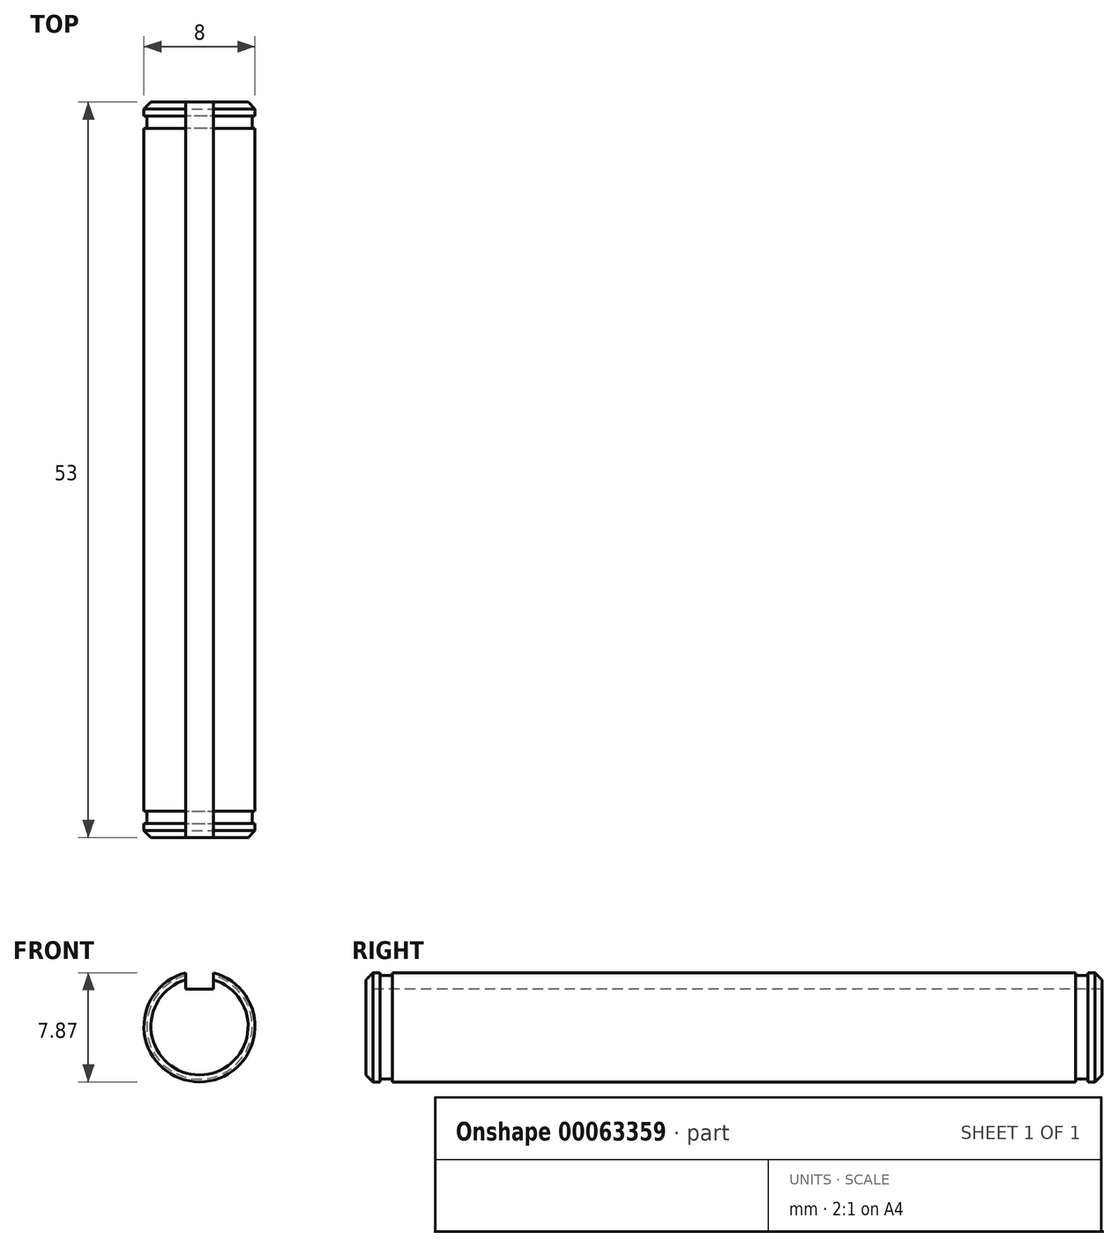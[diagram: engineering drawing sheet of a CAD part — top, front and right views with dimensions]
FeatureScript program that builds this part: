
annotation { "Feature Type Name" : "Feature", "Feature Type Description" : "" }
export const myFeature = defineFeature(function(context is Context, id is Id, definition is map)
    precondition{}
    {
        {
            var Q0;
            Q0=qCreatedBy(makeId("Front.planeOp"),FACE);
            var sketch = newSketch(context, id + "F0", { "sketchPlane" : qUnion([Q0])});
            skCircle(sketch, "E0", {"center": v(0, 0) * mm, "radius": 4 * mm});
            skSolve(sketch);
        }
        {
            var Q0;
            Q0=qSketchRegion(id+"F0",true);
            extrude(context, id + "F1", {"entities" : qUnion([Q0]), "depth" : (48 + 2 * 2.5) * mm});
        }
        {
            var Q0;
            Q0=makeQuery(id+"F1.opExtrude","CAP_FACE",FACE,{"disambiguationData":[OSD([sQuery(id+"F0.wireOp",EDGE,"E0")])],"isStart":false});
            var sketch = newSketch(context, id + "F2", { "sketchPlane" : qUnion([Q0])});
            skLineSegment(sketch, "E1", {"start": v(-1, 5.35) * mm, "end": v(1, 5.35) * mm});
            skLineSegment(sketch, "E2", {"start": v(0, 0) * mm, "end": v(0, 5.35) * mm, "construction": true});
            skLineSegment(sketch, "E3", {"start": v(-1, 2.67) * mm, "end": v(1, 2.67) * mm});
            skPoint(sketch, "E3.startSnap0", {"position": v(0, 2.67) * mm});
            skLineSegment(sketch, "E4", {"start": v(1, 2.67) * mm, "end": v(1, 5.35) * mm});
            skLineSegment(sketch, "E5", {"start": v(-1, 2.67) * mm, "end": v(-1, 5.35) * mm});
            skLineSegment(sketch, "E6", {"start": v(1, 3.87) * mm, "end": v(-1, 3.87) * mm, "construction": true});
            skSolve(sketch);
        }
        {
            var Q0;
            Q0=qSketchRegion(id+"F2",true);
            extrude(context, id + "F3", {"entities" : qUnion([Q0]), "operationType" : NewBodyOperationType.REMOVE, "endBound" : BoundingType.THROUGH_ALL, "oppositeDirection" : true, "depth" : 25 * mm});
        }
        {
            var Q0;
            Q0=makeQuery(id+"F1.opExtrude","CAP_EDGE",EDGE,{"disambiguationData":[OSD([sQuery(id+"F0.wireOp",EDGE,"E0")])],"isStart":false});
            var Q1;
            Q1=makeQuery(id+"F1.opExtrude","CAP_EDGE",EDGE,{"disambiguationData":[OSD([sQuery(id+"F0.wireOp",EDGE,"E0")])],"isStart":true});
            chamfer(context, id + "F4", {"entities" : qUnion([Q0, Q1]), "width" : 0.5 * mm, "tangentPropagation" : true});
        }
        {
            var Q0;
            Q0=makeQuery(id+"F1.opExtrude","CAP_FACE",FACE,{"disambiguationData":[OSD([sQuery(id+"F0.wireOp",EDGE,"E0")])],"isStart":false});
            cPlane(context, id + "F5", {"entities" : qUnion([Q0]), "cplaneType" : CPlaneType.OFFSET, "offset" : 1 * mm, "oppositeDirection" : true, "width" : 150 * mm, "height" : 150 * mm});
        }
        {
            var Q0;
            Q0=qCreatedBy(id+"F5.planeOp",FACE);
            var sketch = newSketch(context, id + "F6", { "sketchPlane" : qUnion([Q0])});
            skCircle(sketch, "E7", {"center": v(0, 0) * mm, "radius": 3.8 * mm});
            skCircle(sketch, "E8", {"center": v(0, 0) * mm, "radius": 5.13 * mm});
            skSolve(sketch);
        }
        {
            var Q0;
            Q0 = qSketchRegion(id + "F6", true);
            extrude(context, id + "F7", {"entities" : qUnion([Q0]), "operationType" : NewBodyOperationType.REMOVE, "oppositeDirection" : true, "depth" : 0.9 * mm});
        }
        {
            var Q0;
            Q0=makeQuery(id+"F1.opExtrude","CAP_FACE",FACE,{"disambiguationData":[OSD([sQuery(id+"F0.wireOp",EDGE,"E0")])],"isStart":true});
            cPlane(context, id + "F8", {"entities" : qUnion([Q0]), "cplaneType" : CPlaneType.OFFSET, "offset" : 1 * mm, "oppositeDirection" : true, "width" : 150 * mm, "height" : 150 * mm});
        }
        {
            var Q0;
            Q0=qCreatedBy(id+"F8.planeOp",FACE);
            var sketch = newSketch(context, id + "F9", { "sketchPlane" : qUnion([Q0])});
            skCircle(sketch, "E9", {"center": v(0, 0) * mm, "radius": 3.8 * mm});
            skCircle(sketch, "E10", {"center": v(0, 0) * mm, "radius": 7.94 * mm});
            skSolve(sketch);
        }
        {
            var Q0;
            Q0 = qSketchRegion(id + "F9", true);
            extrude(context, id + "F10", {"entities" : qUnion([Q0]), "operationType" : NewBodyOperationType.REMOVE, "oppositeDirection" : true, "depth" : 0.9 * mm});
        }
    });
